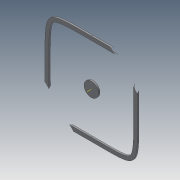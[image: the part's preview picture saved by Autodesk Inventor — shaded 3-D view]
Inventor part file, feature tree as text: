
AUTODESK INVENTOR PART (.ipt)
format: ipt  version: 2014 SP1 (Build 180222100, 222)  size: 148,480 bytes
history: native  units: in
note: dims shown in document units (in); Inventor stores cm internally (conversion verified against a paired STEP export)
features: extrude x1, other x1, sketch x1
ambient origin geometry x8: Origin, YZ Plane, XZ Plane, XY Plane, X Axis, Y Axis, Z Axis, Center Point
bodies: Solid1 (feature_tree)
feature tree (3):
  extrude  "Extrusion1"  Depth=0.27in
  other  "Work Axis1"
  sketch  "Sketch1"  dims[d0=2.6in d1=2.5998in d2=3.25in d3=0.27in d4=0.11in d5=0.0in d6=1.0in]
